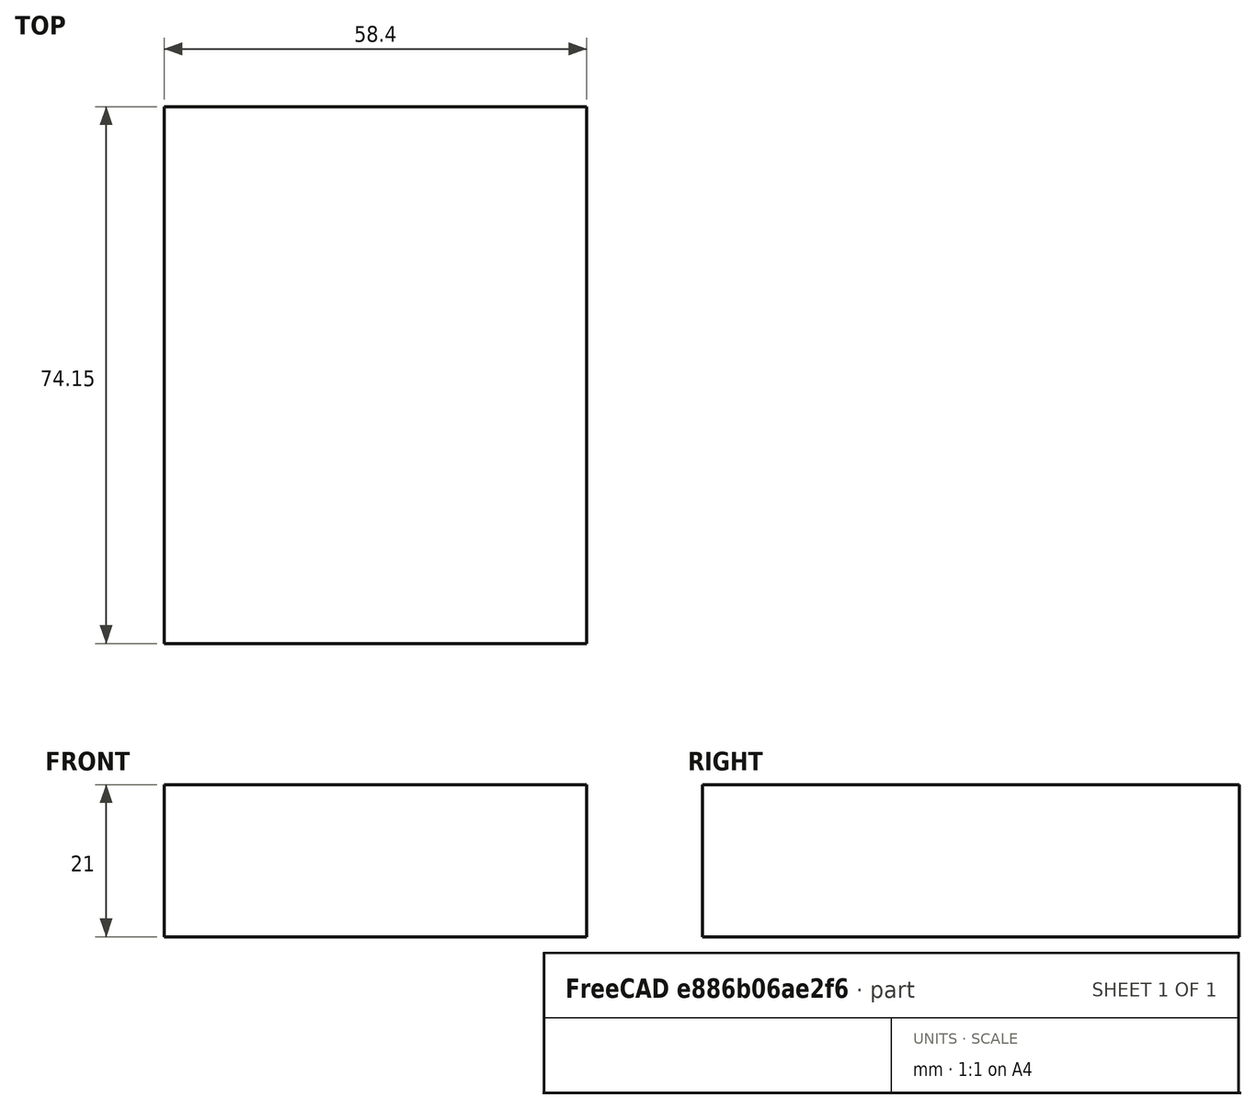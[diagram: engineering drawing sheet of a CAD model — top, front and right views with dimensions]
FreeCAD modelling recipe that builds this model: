
FCSTD DOCUMENT  (FreeCAD 0.21R31917 (Git))
Label: conductor4
License: All rights reserved
LicenseURL: http://en.wikipedia.org/wiki/All_rights_reserved
objects: Sketcher::SketchObject×3, PartDesign::Body×2, PartDesign::Pad×1
note: 7 computed .brp shape members not serialized (recipe doc carries the construction recipe); baked Part::Feature solids carry a one-line shape summary decoded from their .brp

FEATURE [Sketcher::SketchObject] Sketch
  FullyConstrained = false
  MapMode = 5
  Support = -> [XY_Plane]
  sketch-geometry (5):
    g0: LineSegment StartX=-29.198 StartY=54.5286 StartZ=0 EndX=-29.198 EndY=-19.624 EndZ=0
    g1: LineSegment StartX=-29.198 StartY=-19.624 StartZ=0 EndX=29.198 EndY=-19.624 EndZ=0
    g2: LineSegment StartX=29.198 StartY=-19.624 StartZ=0 EndX=29.198 EndY=54.5286 EndZ=0
    g3: LineSegment StartX=29.198 StartY=54.5286 StartZ=0 EndX=-29.198 EndY=54.5286 EndZ=0
    g4: GeomPoint X=0 Y=17.4523 Z=0
  constraints (10):
    c: Coincident(g0,g1)
    c: Coincident(g1,g2)
    c: Coincident(g2,g3)
    c: Coincident(g3,g0)
    c: Horizontal(g1)
    c: Horizontal(g3)
    c: Vertical(g0)
    c: Vertical(g2)
    c: Symmetric(g1,g0,g4)
    c: PointOnObject(g4,g-2)
FEATURE [PartDesign::Pad] Pad
  Direction = (0,0,1)
  Length = 21
  Length2 = 10
  Profile = -> Sketch
  ReferenceAxis = -> Sketch [N_Axis]
  Type = 0
FEATURE [PartDesign::Body] Body
  Group = -> [Sketch,Pad]
  Origin = -> Origin
  Tip = -> Pad
FEATURE [Sketcher::SketchObject] Sketch001
  ExternalGeometry = -> [Sketch]
  FullyConstrained = false
  expr: Constraints[11] = 29 - 3
  sketch-geometry (5):
    g0: LineSegment StartX=-13 StartY=2.66195 StartZ=0 EndX=-13 EndY=54.5286 EndZ=0
    g1: LineSegment StartX=-13 StartY=54.5286 StartZ=0 EndX=13 EndY=54.5286 EndZ=0
    g2: LineSegment StartX=13 StartY=54.5286 StartZ=0 EndX=13 EndY=2.66195 EndZ=0
    g3: LineSegment StartX=13 StartY=2.66195 StartZ=0 EndX=-13 EndY=2.66195 EndZ=0
    g4: GeomPoint X=0 Y=28.5953 Z=0
  constraints (12):
    c: Coincident(g0,g1)
    c: Coincident(g1,g2)
    c: Coincident(g2,g3)
    c: Coincident(g3,g0)
    c: Horizontal(g1)
    c: Horizontal(g3)
    c: Vertical(g0)
    c: Vertical(g2)
    c: Symmetric(g1,g0,g4)
    c: PointOnObject(g4,g-2)
    c: PointOnObject(g1,g-3)
    c: DistanceX(g1,g1) = 26
FEATURE [Sketcher::SketchObject] Sketch002
  FullyConstrained = false
  MapMode = 5
  Support = -> [XY_Plane001]
  sketch-geometry (1):
    g0: Circle CenterX=0 CenterY=0 CenterZ=0 NormalX=0 NormalY=0 NormalZ=1 AngleXU=0 Radius=51.8974
  constraints (1):
    c: Coincident(g0,g-1)
FEATURE [PartDesign::Body] Body001
  Group = -> [Sketch002]
  Origin = -> Origin001
